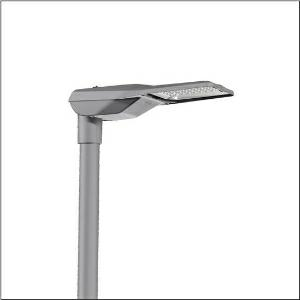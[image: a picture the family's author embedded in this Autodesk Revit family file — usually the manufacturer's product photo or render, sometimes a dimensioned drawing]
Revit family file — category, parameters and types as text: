
# Revit family: streetlight_sl_21_mini___p0_5a_5xe2v33s08jb_bee1
name_source: partatom
category: Lighting Fixtures
units: mm (PartAtom-declared; Revit-internal decimal feet)

## family parameters
Cut with Voids When Loaded = No
Host = Face
Light Source = No
Part Type = Normal
Room Calculation Point = No
Round Connector Dimension = Use Diameter
Shared = No

## types (1)
- --- (1 x LED, 12720 lm, 88.6 W, 3000K)
    Apparent Load = 89 VA
    CIE Flux Codes = 37 73 96 100 100
    Color Rendering = 70
    Color Temperature = 3000K
    Default Elevation = 1800 mm
    Description = Streetlight SL 21 mini, mast luminaire, primary light control with lens, of PMMA, primary optical cover: cover, of toughened safety glass, transparent, light distribution: P0.5a, light emission: direct distribution, primary light characteristic: asymmetric, installation type: post-top, side-entry, LED, High Power LED, rated luminous flux: 12.720lm, luminous efficacy: 144lm/W, light colour: 730, colour temperature: 3000K, control gear: D4i, control: pre-setting: logarithmic dimming characteristic, flexible luminous flux parameterisation, time-dependent luminous flux control, constant luminous flux control, overheat protection, mains connection: 220..240V, AC, 50/60Hz, start of lifetime: 89W, end of service life: 92W, reduction: 41W, luminaire housing, of diecast aluminium, powder-coated, Siteco® metallic grey (DB 702S), corrosivity category C5 mid according to DIN EN ISO 12944, multi-level sealing system, sealing non-destructively replaceable, inclination adjustable: 0°, 5°, 10°, 15°, please order mast flange separately, length: 628mm, width: 235mm, height: 110mm, mast flange for spigot size: 42mm (side-entry): 5XC10008XM4, 60/48mm (side-entry/post-top): 5XC10108XM2, 76/60mm (side-entry/post-top): 5XC10108XM1, mounting height: 4..8m, Smart Interface above, protection rating (complete): IP66, insulation class (complete): insulation class II (safety insulation), certification: CE, ENEC, ENEC+, VDE, impact resistance: IK10, permissible operating ambient temperature for outdoor applications: -40..+50°C, standard-compliant lighting for roads and squares, packaging unit: 1 piece

Light Distribution: P0.5a
    Height = 110 mm
    Lamp = 1 x LED
    Lamp Light Flux = 12720 lm
    Lamp Power = 88.6 W
    Lamp count = 1
    Length = 625 mm
    Luminous efficacy = 144 lm/W
    Manufacturer = Siteco
    ModVariant = No
    Model = 5XE2V33S08JB
    Number of Poles = 1
    OnlyDefault = Yes
    Power Factor = 1
    Product Name = Streetlight SL 21 mini | P0.5a
    Product group = mast luminaire | pylon top
    ProductGroupID = 6100
    Protection Class = Protection class II
    Protection Degree = IP 66
    RLX_Detail_Level = 1
    RLX_Emergency_Light_Flux = 0 lm
    RLX_Emergency_Type = 0
    RLX_Emergency_Type_DB = No
    RlxData = <blob elided: 25965 chars, md5=283ca123>
    Socket = socket
    Standby Power = 0 W
    System Light Flux = 12720 lm
    System Power = 89 W
    Type Comments = factory setting: luminous flux: 100 % | dim-lin: 254 | 915 mA
    Type Image = l_1003515.jpg
    URL = http://relux.com
    VarID = @adj_032977
    Voltage = 0 V
    Weight = 0.00 kg
    Width = 234 mm

## geometry (parser evidence)
native form markers: Blend x4, Sweep x11
no freeform markers — native parametric forms only
